# Revit family: 702-30-103-DN50-150
name_source: partatom
category: Pipe Accessories
units: mm (PartAtom-declared; Revit-internal decimal feet)

## family parameters
Always vertical = Yes
Cut with Voids When Loaded = No
Part Type = Valve - Breaks Into
Round Connector Dimension = Use Diameter
Shared = No
Work Plane-Based = No

## types (6) — shared parameters
DN050_PN10/16 = 702-050-30-134
DN065_PN10/16 = 702-065-30-134
DN080_PN10/16 = 702-080-30-134
DN100_PN10/16 = 702-100-30-134
DN125_PN10/16 = 702-125-30-134
DN150_PN10/16 = 702-150-30-134
Description_ = AVK KNIFE GATE VALVE
Flange_Thickness = 5 mm  [stored 0.0164042 ft]
HW_Dia = 20 mm  [stored 0.0656168 ft]
Neck_Rod = 10 mm  [stored 0.0328084 ft]
Neck_Rod_2 = 20 mm  [stored 0.0656168 ft]
Neck_Rod_3 = 5 mm  [stored 0.0164042 ft]
Search_table = 702-30-103-DN50-150
URL product pages = https://www.avkvalves.com

## per-type parameters (varying)
| type | B2_Ref | Body_width | Body_width_2 | Bonnet_height | Bonnet_height_2 | D | Fillet_Radius | H3 | HW_Rib | H_Ref | Hc | Hc_Ref | Ho | ID | L | L2 | N_height | Name_Ref | Nominal Diameter (DN) | W | W1 | W2 | W3 |
| DN 050 | 78 mm  [stored 0.255906 ft] | 87 mm | 69 mm  [stored 0.226378 ft] | 330 mm | 182 mm | 78 mm  [stored 0.255906 ft] | 5 mm  [stored 0.0164042 ft] | 687 mm | 145 mm | 113 mm | 363 mm | 353 mm | 592 mm | 25 mm  [stored 0.082021 ft] | 43 mm  [stored 0.141076 ft] | 47 mm | 141 mm | 169 mm | 50 mm  [stored 0.164042 ft] | 130 mm | 402 mm | 65 mm  [stored 0.213255 ft] | 54 mm |
| DN 065 | 86 mm | 95 mm | 76 mm | 359 mm | 198 mm | 78 mm  [stored 0.255906 ft] | 5 mm  [stored 0.0164042 ft] | 792 mm | 145 mm | 124 mm | 395 mm | 385 mm | 720 mm | 33 mm | 46 mm  [stored 0.150919 ft] | 51 mm  [stored 0.167323 ft] | 194 mm | 186 mm | 65 mm  [stored 0.213255 ft] | 143 mm | 503 mm | 72 mm | 60 mm  [stored 0.19685 ft] |
| DN 080 | 110 mm | 122 mm | 98 mm | 392 mm | 216 mm | 103 mm | 5 mm  [stored 0.0164042 ft] | 910 mm | 195 mm | 159 mm | 431 mm | 421 mm | 758 mm | 40 mm  [stored 0.131234 ft] | 46 mm  [stored 0.150919 ft] | 51 mm  [stored 0.167323 ft] | 196 mm | 238 mm | 80 mm  [stored 0.262467 ft] | 183 mm | 601 mm | 92 mm | 76 mm |
| DN 100 | 121 mm | 135 mm | 108 mm | 432 mm | 238 mm | 103 mm | 10 mm  [stored 0.0328084 ft] | 933 mm | 195 mm | 175 mm | 475 mm | 465 mm | 831 mm | 50 mm  [stored 0.164042 ft] | 52 mm | 57 mm | 211 mm | 263 mm | 100 mm  [stored 0.328084 ft] | 202 mm | 703 mm | 101 mm  [stored 0.331365 ft] | 84 mm |
| DN 125 | 137 mm | 153 mm | 122 mm | 480 mm | 264 mm | 103 mm | 10 mm  [stored 0.0328084 ft] | 1028 mm | 195 mm | 198 mm | 528 mm | 518 mm | 913 mm | 63 mm | 56 mm  [stored 0.183727 ft] | 62 mm | 227 mm | 298 mm | 125 mm | 229 mm | 804 mm | 115 mm | 95 mm |
| DN 150 | 160 mm | 178 mm | 142 mm | 609 mm | 335 mm | 140 mm | 10 mm  [stored 0.0328084 ft] | 1297 mm | 270 mm | 231 mm | 670 mm | 660 mm | 1162 mm | 75 mm | 56 mm  [stored 0.183727 ft] | 62 mm | 286 mm | 347 mm | 150 mm | 267 mm | 1003 mm | 134 mm | 111 mm |

note: [stored X ft] marks values corroborated as IEEE doubles in the binary element streams (Revit-internal decimal feet)

## geometry (parser evidence)
native form markers: Sweep x6
no freeform markers — native parametric forms only
